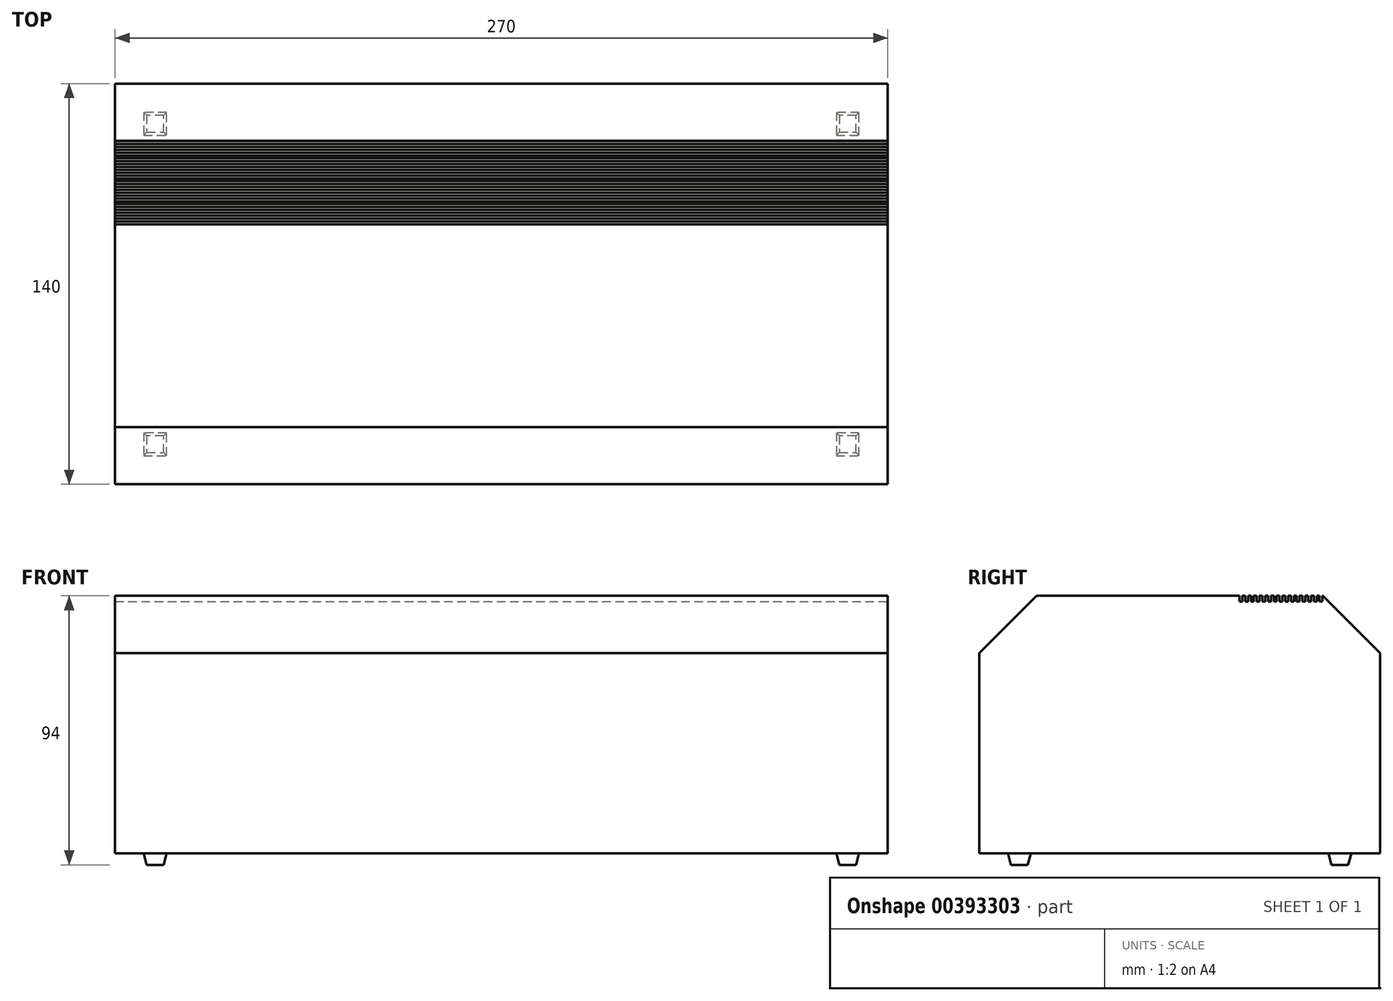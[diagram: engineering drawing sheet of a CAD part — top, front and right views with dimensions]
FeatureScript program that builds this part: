
annotation { "Feature Type Name" : "Feature", "Feature Type Description" : "" }
export const myFeature = defineFeature(function(context is Context, id is Id, definition is map)
    precondition{}
    {
        {
            var Q0;
            Q0=qCreatedBy(makeId("Top.planeOp"),FACE);
            var sketch = newSketch(context, id + "F0", { "sketchPlane" : qUnion([Q0])});
            skLineSegment(sketch, "E0.bottom", {"start": v(135, -70) * mm, "end": v(-135, -70) * mm});
            skLineSegment(sketch, "E0.top", {"start": v(135, 70) * mm, "end": v(-135, 70) * mm});
            skLineSegment(sketch, "E0.left", {"start": v(135, -70) * mm, "end": v(135, 70) * mm});
            skLineSegment(sketch, "E0.right", {"start": v(-135, -70) * mm, "end": v(-135, 70) * mm});
            skPoint(sketch, "E0.middle", {"position": v(0, 0) * mm});
            skSolve(sketch);
        }
        {
            var Q0;
            Q0 = qSketchRegion(id + "F0", true);
            extrude(context, id + "F1", {"entities" : qUnion([Q0]), "depth" : 90 * mm});
        }
        {
            var Q0;
            Q0=makeQuery(id+"F1.opExtrude","CAP_EDGE",EDGE,{"disambiguationData":[OSD([sQuery(id+"F0.wireOp",EDGE,"E0.bottom")])],"isStart":false});
            var Q1;
            Q1=makeQuery(id+"F1.opExtrude","CAP_EDGE",EDGE,{"disambiguationData":[OSD([sQuery(id+"F0.wireOp",EDGE,"E0.top")])],"isStart":false});
            chamfer(context, id + "F2", {"entities" : qUnion([Q0, Q1]), "width" : 20 * mm, "tangentPropagation" : true});
        }
        {
            var Q0;
            Q0=makeQuery(id+"F1.opExtrude","SWEPT_FACE",FACE,{"disambiguationData":[OSD([sQuery(id+"F0.wireOp",EDGE,"E0.left")])]});
            var sketch = newSketch(context, id + "F3", { "sketchPlane" : qUnion([Q0])});
            skLineSegment(sketch, "E1.bottom", {"start": v(20.9, 90) * mm, "end": v(21.9, 90) * mm});
            skLineSegment(sketch, "E1.top", {"start": v(20.9, 88) * mm, "end": v(21.9, 88) * mm});
            skLineSegment(sketch, "E1.left", {"start": v(20.9, 90) * mm, "end": v(20.9, 88) * mm});
            skLineSegment(sketch, "E1.right", {"start": v(21.9, 90) * mm, "end": v(21.9, 88) * mm});
            skLineSegment(sketch, "E2.1.0.0", {"start": v(23.9, 90) * mm, "end": v(23.9, 88) * mm});
            skLineSegment(sketch, "E2.1.0.1", {"start": v(22.9, 90) * mm, "end": v(23.9, 90) * mm});
            skLineSegment(sketch, "E2.1.0.2", {"start": v(22.9, 90) * mm, "end": v(22.9, 88) * mm});
            skLineSegment(sketch, "E2.1.0.3", {"start": v(22.9, 88) * mm, "end": v(23.9, 88) * mm});
            skLineSegment(sketch, "E2.2.0.0", {"start": v(25.9, 90) * mm, "end": v(25.9, 88) * mm});
            skLineSegment(sketch, "E2.2.0.1", {"start": v(24.9, 90) * mm, "end": v(25.9, 90) * mm});
            skLineSegment(sketch, "E2.2.0.2", {"start": v(24.9, 90) * mm, "end": v(24.9, 88) * mm});
            skLineSegment(sketch, "E2.2.0.3", {"start": v(24.9, 88) * mm, "end": v(25.9, 88) * mm});
            skLineSegment(sketch, "E2.3.0.0", {"start": v(27.9, 90) * mm, "end": v(27.9, 88) * mm});
            skLineSegment(sketch, "E2.3.0.1", {"start": v(26.9, 90) * mm, "end": v(27.9, 90) * mm});
            skLineSegment(sketch, "E2.3.0.2", {"start": v(26.9, 90) * mm, "end": v(26.9, 88) * mm});
            skLineSegment(sketch, "E2.3.0.3", {"start": v(26.9, 88) * mm, "end": v(27.9, 88) * mm});
            skLineSegment(sketch, "E2.4.0.0", {"start": v(29.9, 90) * mm, "end": v(29.9, 88) * mm});
            skLineSegment(sketch, "E2.4.0.1", {"start": v(28.9, 90) * mm, "end": v(29.9, 90) * mm});
            skLineSegment(sketch, "E2.4.0.2", {"start": v(28.9, 90) * mm, "end": v(28.9, 88) * mm});
            skLineSegment(sketch, "E2.4.0.3", {"start": v(28.9, 88) * mm, "end": v(29.9, 88) * mm});
            skLineSegment(sketch, "E2.5.0.0", {"start": v(31.9, 90) * mm, "end": v(31.9, 88) * mm});
            skLineSegment(sketch, "E2.5.0.1", {"start": v(30.9, 90) * mm, "end": v(31.9, 90) * mm});
            skLineSegment(sketch, "E2.5.0.2", {"start": v(30.9, 90) * mm, "end": v(30.9, 88) * mm});
            skLineSegment(sketch, "E2.5.0.3", {"start": v(30.9, 88) * mm, "end": v(31.9, 88) * mm});
            skLineSegment(sketch, "E2.6.0.0", {"start": v(33.9, 90) * mm, "end": v(33.9, 88) * mm});
            skLineSegment(sketch, "E2.6.0.1", {"start": v(32.9, 90) * mm, "end": v(33.9, 90) * mm});
            skLineSegment(sketch, "E2.6.0.2", {"start": v(32.9, 90) * mm, "end": v(32.9, 88) * mm});
            skLineSegment(sketch, "E2.6.0.3", {"start": v(32.9, 88) * mm, "end": v(33.9, 88) * mm});
            skLineSegment(sketch, "E2.7.0.0", {"start": v(35.9, 90) * mm, "end": v(35.9, 88) * mm});
            skLineSegment(sketch, "E2.7.0.1", {"start": v(34.9, 90) * mm, "end": v(35.9, 90) * mm});
            skLineSegment(sketch, "E2.7.0.2", {"start": v(34.9, 90) * mm, "end": v(34.9, 88) * mm});
            skLineSegment(sketch, "E2.7.0.3", {"start": v(34.9, 88) * mm, "end": v(35.9, 88) * mm});
            skLineSegment(sketch, "E2.8.0.0", {"start": v(37.9, 90) * mm, "end": v(37.9, 88) * mm});
            skLineSegment(sketch, "E2.8.0.1", {"start": v(36.9, 90) * mm, "end": v(37.9, 90) * mm});
            skLineSegment(sketch, "E2.8.0.2", {"start": v(36.9, 90) * mm, "end": v(36.9, 88) * mm});
            skLineSegment(sketch, "E2.8.0.3", {"start": v(36.9, 88) * mm, "end": v(37.9, 88) * mm});
            skLineSegment(sketch, "E2.9.0.0", {"start": v(39.9, 90) * mm, "end": v(39.9, 88) * mm});
            skLineSegment(sketch, "E2.9.0.1", {"start": v(38.9, 90) * mm, "end": v(39.9, 90) * mm});
            skLineSegment(sketch, "E2.9.0.2", {"start": v(38.9, 90) * mm, "end": v(38.9, 88) * mm});
            skLineSegment(sketch, "E2.9.0.3", {"start": v(38.9, 88) * mm, "end": v(39.9, 88) * mm});
            skLineSegment(sketch, "E2.10.0.0", {"start": v(41.9, 90) * mm, "end": v(41.9, 88) * mm});
            skLineSegment(sketch, "E2.10.0.1", {"start": v(40.9, 90) * mm, "end": v(41.9, 90) * mm});
            skLineSegment(sketch, "E2.10.0.2", {"start": v(40.9, 90) * mm, "end": v(40.9, 88) * mm});
            skLineSegment(sketch, "E2.10.0.3", {"start": v(40.9, 88) * mm, "end": v(41.9, 88) * mm});
            skLineSegment(sketch, "E2.11.0.0", {"start": v(43.9, 90) * mm, "end": v(43.9, 88) * mm});
            skLineSegment(sketch, "E2.11.0.1", {"start": v(42.9, 90) * mm, "end": v(43.9, 90) * mm});
            skLineSegment(sketch, "E2.11.0.2", {"start": v(42.9, 90) * mm, "end": v(42.9, 88) * mm});
            skLineSegment(sketch, "E2.11.0.3", {"start": v(42.9, 88) * mm, "end": v(43.9, 88) * mm});
            skLineSegment(sketch, "E2.12.0.0", {"start": v(45.9, 90) * mm, "end": v(45.9, 88) * mm});
            skLineSegment(sketch, "E2.12.0.1", {"start": v(44.9, 90) * mm, "end": v(45.9, 90) * mm});
            skLineSegment(sketch, "E2.12.0.2", {"start": v(44.9, 90) * mm, "end": v(44.9, 88) * mm});
            skLineSegment(sketch, "E2.12.0.3", {"start": v(44.9, 88) * mm, "end": v(45.9, 88) * mm});
            skLineSegment(sketch, "E2.13.0.0", {"start": v(47.9, 90) * mm, "end": v(47.9, 88) * mm});
            skLineSegment(sketch, "E2.13.0.1", {"start": v(46.9, 90) * mm, "end": v(47.9, 90) * mm});
            skLineSegment(sketch, "E2.13.0.2", {"start": v(46.9, 90) * mm, "end": v(46.9, 88) * mm});
            skLineSegment(sketch, "E2.13.0.3", {"start": v(46.9, 88) * mm, "end": v(47.9, 88) * mm});
            skLineSegment(sketch, "E2.14.0.0", {"start": v(49.9, 90) * mm, "end": v(49.9, 88) * mm});
            skLineSegment(sketch, "E2.14.0.1", {"start": v(48.9, 90) * mm, "end": v(49.9, 90) * mm});
            skLineSegment(sketch, "E2.14.0.2", {"start": v(48.9, 90) * mm, "end": v(48.9, 88) * mm});
            skLineSegment(sketch, "E2.14.0.3", {"start": v(48.9, 88) * mm, "end": v(49.9, 88) * mm});
            skLineSegment(sketch, "E2.direction1", {"start": v(20.9, 88) * mm, "end": v(22.9, 88) * mm, "construction": true});
            skSolve(sketch);
        }
        {
            var Q0;
            Q0=makeQuery(id+"F3.imprint","IMPRINT",FACE,{"disambiguationData":[TD([[makeQuery(id+"F3.imprint","IMPRINT",EDGE,{"derivedFrom":sQuery(id+"F3.wireOp",EDGE,"E1.bottom")}),-1.0]])]});
            var Q1;
            Q1 = qSketchRegion(id + "F3", true);
            var Q2;
            Q2=makeQuery(id+"F1.opExtrude","SWEPT_FACE",FACE,{"disambiguationData":[OSD([sQuery(id+"F0.wireOp",EDGE,"E0.right")])]});
            extrude(context, id + "F4", {"entities" : qUnion([Q0, Q1]), "operationType" : NewBodyOperationType.REMOVE, "endBound" : BoundingType.UP_TO_SURFACE, "oppositeDirection" : true, "endBoundEntityFace" : qUnion([Q2]), "depth" : 25 * mm});
        }
        {
            var Q0;
            Q0=makeQuery(id+"F1.opExtrude","CAP_FACE",FACE,{"disambiguationData":[OSD([sQuery(id+"F0.wireOp",EDGE,"E0.bottom"),sQuery(id+"F0.wireOp",EDGE,"E0.top"),sQuery(id+"F0.wireOp",EDGE,"E0.left"),sQuery(id+"F0.wireOp",EDGE,"E0.right"),sQuery(id+"F0.wireOp",EDGE,"LXP78e7o-w7LA-LCvA-ul7r-NfpQnvCYBzEu.bottom"),sQuery(id+"F0.wireOp",EDGE,"LXP78e7o-w7LA-LCvA-ul7r-NfpQnvCYBzEu.top"),sQuery(id+"F0.wireOp",EDGE,"LXP78e7o-w7LA-LCvA-ul7r-NfpQnvCYBzEu.left"),sQuery(id+"F0.wireOp",EDGE,"LXP78e7o-w7LA-LCvA-ul7r-NfpQnvCYBzEu.right")])],"isStart":true});
            var sketch = newSketch(context, id + "F5", { "sketchPlane" : qUnion([Q0])});
            skLineSegment(sketch, "E3.bottom", {"start": v(125, 52) * mm, "end": v(117, 52) * mm});
            skLineSegment(sketch, "E3.top", {"start": v(125, 60) * mm, "end": v(117, 60) * mm});
            skLineSegment(sketch, "E3.left", {"start": v(125, 52) * mm, "end": v(125, 60) * mm});
            skLineSegment(sketch, "E3.right", {"start": v(117, 52) * mm, "end": v(117, 60) * mm});
            skLineSegment(sketch, "E4.MirrorCS", {"start": v(125, -52) * mm, "end": v(125, -60) * mm});
            skLineSegment(sketch, "E5.MirrorCS", {"start": v(125, -52) * mm, "end": v(117, -52) * mm});
            skLineSegment(sketch, "E6.MirrorCS", {"start": v(125, -60) * mm, "end": v(117, -60) * mm});
            skLineSegment(sketch, "E7.MirrorCS", {"start": v(117, -52) * mm, "end": v(117, -60) * mm});
            skLineSegment(sketch, "E8.MirrorCS", {"start": v(-125, 60) * mm, "end": v(-117, 60) * mm});
            skLineSegment(sketch, "E9.MirrorCS", {"start": v(-125, 52) * mm, "end": v(-125, 60) * mm});
            skLineSegment(sketch, "E10.MirrorCS", {"start": v(-117, 52) * mm, "end": v(-117, 60) * mm});
            skLineSegment(sketch, "E11.MirrorCS", {"start": v(-125, 52) * mm, "end": v(-117, 52) * mm});
            skLineSegment(sketch, "E12.MirrorCS", {"start": v(-125, -52) * mm, "end": v(-117, -52) * mm});
            skLineSegment(sketch, "E13.MirrorCS", {"start": v(-117, -52) * mm, "end": v(-117, -60) * mm});
            skLineSegment(sketch, "E14.MirrorCS", {"start": v(-125, -60) * mm, "end": v(-117, -60) * mm});
            skLineSegment(sketch, "E15.MirrorCS", {"start": v(-125, -52) * mm, "end": v(-125, -60) * mm});
            skSolve(sketch);
        }
        {
            var Q0;
            Q0=makeQuery(id+"F5.imprint","IMPRINT",FACE,{"disambiguationData":[TD([[makeQuery(id+"F5.imprint","IMPRINT",EDGE,{"derivedFrom":sQuery(id+"F5.wireOp",EDGE,"E3.bottom")}),-1.0]])]});
            var Q1;
            Q1=makeQuery(id+"F5.imprint","IMPRINT",FACE,{"disambiguationData":[TD([[makeQuery(id+"F5.imprint","IMPRINT",EDGE,{"derivedFrom":sQuery(id+"F5.wireOp",EDGE,"E4.MirrorCS")}),-1.0]])]});
            var Q2;
            Q2=makeQuery(id+"F5.imprint","IMPRINT",FACE,{"disambiguationData":[TD([[makeQuery(id+"F5.imprint","IMPRINT",EDGE,{"derivedFrom":sQuery(id+"F5.wireOp",EDGE,"E8.MirrorCS")}),-1.0]])]});
            var Q3;
            Q3=makeQuery(id+"F5.imprint","IMPRINT",FACE,{"disambiguationData":[TD([[makeQuery(id+"F5.imprint","IMPRINT",EDGE,{"derivedFrom":sQuery(id+"F5.wireOp",EDGE,"E12.MirrorCS")}),-1.0]])]});
            extrude(context, id + "F6", {"entities" : qUnion([Q0, Q1, Q2, Q3]), "operationType" : NewBodyOperationType.ADD, "depth" : 4 * mm, "hasDraft" : true, "draftAngle" : 15 * degree, "draftPullDirection" : true});
        }
    });
